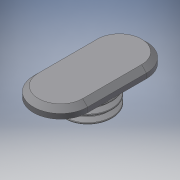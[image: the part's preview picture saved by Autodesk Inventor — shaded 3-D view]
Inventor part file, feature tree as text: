
AUTODESK INVENTOR PART (.ipt)
format: ipt  version: 2016 SP2 (Build 200236200, 236)  size: 390,656 bytes
history: native  units: mm
features: sketch x5, other x4
ambient origin geometry x8: Origin, YZ Plane, XZ Plane, XY Plane, X Axis, Y Axis, Z Axis, Center Point
bodies: Volumenkörper1 (feature_tree), Volumenkörper2 (feature_tree)
feature tree (9):
  other  "Screw-right.ipt"
  other  "Volumenkörper1::Screw-right.ipt"
  other  "Volumenkörper2::Screw-right.ipt"
  other  "Bezeichnung1"
  sketch  "Skizze1"  dims[d0=10.0mm]
  sketch  "Skizze2"
  sketch  "Skizze3"
  sketch  "Skizze4"
  sketch  "Skizze5"
